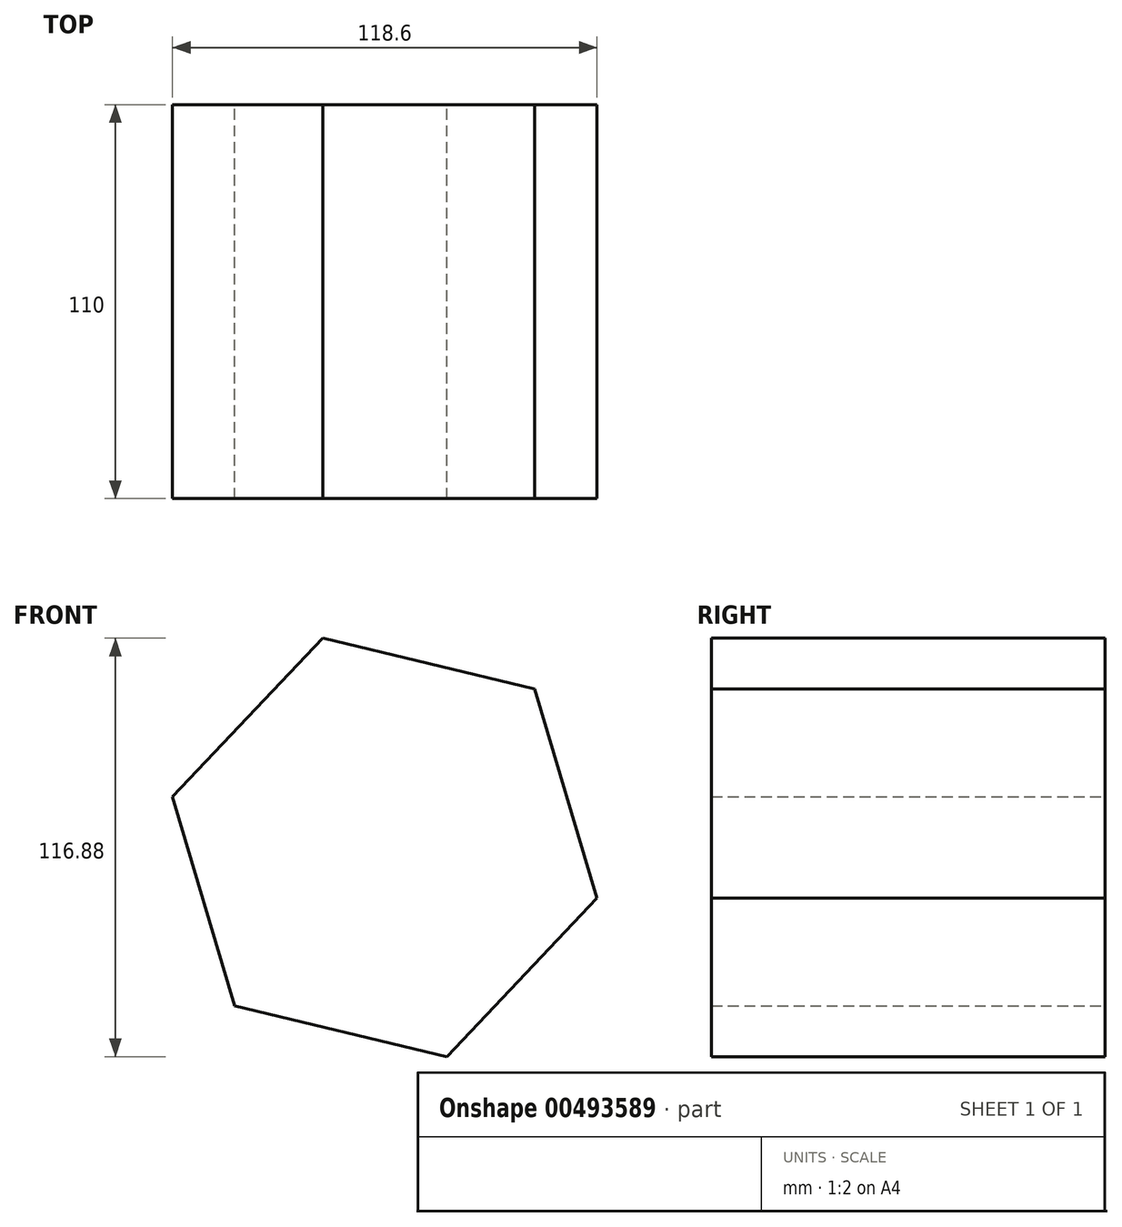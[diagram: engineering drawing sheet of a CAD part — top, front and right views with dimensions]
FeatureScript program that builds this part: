
annotation { "Feature Type Name" : "Feature", "Feature Type Description" : "" }
export const myFeature = defineFeature(function(context is Context, id is Id, definition is map)
    precondition{}
    {
        {
            var Q0;
            Q0=qCreatedBy(makeId("Front.planeOp"),FACE);
            var sketch = newSketch(context, id + "F0", { "sketchPlane" : qUnion([Q0])});
            skCircle(sketch, "E0.cCircle", {"center": v(0, 0) * mm, "radius": 60.97 * mm, "construction": true});
            skLineSegment(sketch, "E0.0", {"start": v(-41.92, -44.27) * mm, "end": v(-59.3, 14.16) * mm});
            skLineSegment(sketch, "E0.1", {"start": v(-59.3, 14.16) * mm, "end": v(-17.38, 58.44) * mm});
            skLineSegment(sketch, "E0.2", {"start": v(-17.38, 58.44) * mm, "end": v(41.92, 44.27) * mm});
            skLineSegment(sketch, "E0.3", {"start": v(41.92, 44.27) * mm, "end": v(59.3, -14.16) * mm});
            skLineSegment(sketch, "E0.4", {"start": v(59.3, -14.16) * mm, "end": v(17.38, -58.44) * mm});
            skLineSegment(sketch, "E0.5", {"start": v(17.38, -58.44) * mm, "end": v(-41.92, -44.27) * mm});
            skSolve(sketch);
        }
        {
            var Q0;
            Q0=makeQuery(id+"F0.imprint","IMPRINT",FACE,{"disambiguationData":[TD([[makeQuery(id+"F0.imprint","IMPRINT",EDGE,{"derivedFrom":sQuery(id+"F0.wireOp",EDGE,"E0.0")}),-1.0]])]});
            extrude(context, id + "F1", {"entities" : qUnion([Q0]), "endBound" : BoundingType.SYMMETRIC, "depth" : 110 * mm});
        }
    });
